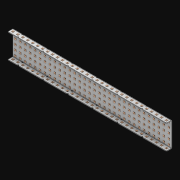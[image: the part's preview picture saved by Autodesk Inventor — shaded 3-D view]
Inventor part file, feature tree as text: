
AUTODESK INVENTOR PART (.ipt)
format: ipt  version: 2021 (Build 250183000, 183)  size: 3,855,872 bytes
history: native  units: in
note: dims shown in document units (in); Inventor stores cm internally (conversion verified against a paired STEP export)
features: extrude x225, other x224, sketch x4, thicken_offset x3, pattern_linear x3, imported_body x1
ambient origin geometry x8: Origin, YZ Plane, XZ Plane, XY Plane, X Axis, Y Axis, Z Axis, Center Point
bodies: Solid1 (feature_tree)
feature tree (460):
  thicken_offset  "Thicken1"
  thicken_offset  "Thicken2"
  thicken_offset  "Thicken3"
  pattern_linear  "Rectangular Pattern1"  Spacing1=0.001in  [1 undecoded]
  pattern_linear  "Rectangular Pattern2"  Spacing1=0.001in  [1 undecoded]
  pattern_linear  "Rectangular Pattern3"  Spacing1=0.182in  [1 undecoded]
  extrude  "Extrusion1"  Depth=0.063in TaperAngle=0.0deg
  sketch  "Sketch1"  dims[d0=0.001in]
  other  "Srf1"
  sketch  "Sketch2"  dims[d1=0.001in]
  other  "Srf2"
  sketch  "Sketch3"  dims[d2=0.001in]
  other  "Srf3"
  other  "Srf4"
  other  "Srf5"
  other  "Srf6"
  other  "Srf7"
  other  "Srf8"
  other  "Srf9"
  other  "Srf10"
  other  "Srf11"
  other  "Srf12"
  other  "Srf13"
  other  "Srf14"
  other  "Srf15"
  other  "Srf16"
  other  "Srf17"
  other  "Srf18"
  other  "Srf19"
  other  "Srf20"
  other  "Srf21"
  other  "Srf22"
  other  "Srf23"
  other  "Srf24"
  other  "Srf25"
  other  "Srf26"
  other  "Srf27"
  other  "Srf28"
  other  "Srf29"
  other  "Srf30"
  other  "Srf31"
  other  "Srf32"
  other  "Srf33"
  other  "Srf34"
  other  "Srf38"
  other  "Srf39"
  other  "Srf40"
  other  "Srf41"
  other  "Srf42"
  other  "Srf43"
  other  "Srf44"
  other  "Srf45"
  other  "Srf46"
  other  "Srf47"
  other  "Srf48"
  other  "Srf49"
  other  "Srf50"
  other  "Srf51"
  other  "Srf52"
  other  "Srf53"
  other  "Srf54"
  other  "Srf55"
  other  "Srf56"
  other  "Srf57"
  other  "Srf58"
  other  "Srf59"
  other  "Srf60"
  other  "Srf61"
  other  "Srf62"
  other  "Srf63"
  other  "Srf64"
  other  "Srf65"
  other  "Srf66"
  other  "Srf67"
  other  "Srf68"
  other  "Srf72"
  other  "Srf73"
  other  "Srf74"
  other  "Srf75"
  other  "Srf76"
  other  "Srf77"
  other  "Srf78"
  other  "Srf79"
  other  "Srf80"
  other  "Srf81"
  other  "Srf82"
  other  "Srf83"
  other  "Srf84"
  other  "Srf85"
  other  "Srf86"
  other  "Srf87"
  other  "Srf88"
  other  "Srf89"
  other  "Srf90"
  other  "Srf91"
  other  "Srf92"
  other  "Srf93"
  other  "Srf94"
  other  "Srf95"
  other  "Srf96"
  other  "Srf97"
  other  "Srf98"
  other  "Srf99"
  other  "Srf100"
  other  "Srf101"
  other  "Srf102"
  other  "Srf106"
  other  "Srf107"
  other  "Srf108"
  other  "Srf109"
  other  "Srf110"
  other  "Srf111"
  other  "Srf112"
  other  "Srf113"
  other  "Srf114"
  other  "Srf115"
  other  "Srf116"
  other  "Srf117"
  other  "Srf118"
  other  "Srf119"
  other  "Srf120"
  other  "Srf121"
  other  "Srf122"
  other  "Srf123"
  other  "Srf124"
  other  "Srf125"
  other  "Srf126"
  other  "Srf127"
  other  "Srf128"
  other  "Srf129"
  other  "Srf130"
  other  "Srf131"
  other  "Srf132"
  other  "Srf133"
  other  "Srf134"
  other  "Srf135"
  other  "Srf136"
  other  "Srf137"
  other  "Srf141"
  other  "Srf142"
  other  "Srf143"
  other  "Srf144"
  other  "Srf145"
  other  "Srf146"
  other  "Srf147"
  other  "Srf148"
  other  "Srf149"
  other  "Srf150"
  other  "Srf151"
  other  "Srf152"
  other  "Srf153"
  other  "Srf154"
  other  "Srf155"
  other  "Srf156"
  other  "Srf157"
  other  "Srf158"
  other  "Srf159"
  other  "Srf160"
  other  "Srf161"
  other  "Srf162"
  other  "Srf163"
  other  "Srf164"
  other  "Srf165"
  other  "Srf166"
  other  "Srf167"
  other  "Srf168"
  other  "Srf169"
  other  "Srf170"
  other  "Srf171"
  other  "Srf172"
  other  "Srf176"
  other  "Srf177"
  other  "Srf178"
  other  "Srf179"
  other  "Srf180"
  other  "Srf181"
  other  "Srf182"
  other  "Srf183"
  other  "Srf184"
  other  "Srf185"
  other  "Srf186"
  other  "Srf187"
  other  "Srf188"
  other  "Srf189"
  other  "Srf190"
  other  "Srf191"
  other  "Srf192"
  other  "Srf193"
  other  "Srf194"
  other  "Srf195"
  other  "Srf196"
  other  "Srf197"
  other  "Srf198"
  other  "Srf199"
  other  "Srf200"
  other  "Srf201"
  other  "Srf202"
  other  "Srf203"
  other  "Srf204"
  other  "Srf205"
  other  "Srf206"
  other  "Srf207"
  other  "Srf211"
  other  "Srf212"
  other  "Srf213"
  other  "Srf214"
  other  "Srf215"
  other  "Srf216"
  other  "Srf217"
  other  "Srf218"
  other  "Srf219"
  other  "Srf220"
  other  "Srf221"
  other  "Srf222"
  other  "Srf223"
  other  "Srf224"
  other  "Srf225"
  other  "Srf226"
  other  "Srf227"
  other  "Srf228"
  other  "Srf229"
  other  "Srf230"
  other  "Srf231"
  other  "Srf232"
  other  "Srf233"
  other  "Srf234"
  other  "Srf235"
  other  "Srf236"
  other  "Srf237"
  other  "Srf238"
  other  "Srf239"
  other  "Srf240"
  other  "Srf241"
  other  "Srf242"
  sketch  "Sketch4"  dims[d3=0.001in d4=0.001in d5=0.001in d6=0.182in d7=0.063in d8=0.0in d9=0.182in d10=0.063in d11=0.0in d12=0.182in d13=0.063in d14=0.0in d17=0.5in d18=12.5984in d20=0.5in d21=12.5984in d23=0.5in d24=1.9685in d26=0.5in d27=1.5in d28=0.0in]
  imported_body  "Imported1"
  extrude  "ExtrusionSrf1"  Depth=1.5in
  extrude  "ExtrusionSrf2"  Depth=0.063in TaperAngle=0.0deg
  extrude  "ExtrusionSrf3"  Depth=1.5in
  extrude  "ExtrusionSrf4"  Depth=0.063in TaperAngle=0.0deg
  extrude  "ExtrusionSrf5"  Depth=0.5in
  extrude  "ExtrusionSrf6"  Depth=1.5in
  extrude  "ExtrusionSrf7"  Depth=0.5in
  extrude  "ExtrusionSrf8"  Depth=1.5in
  extrude  "ExtrusionSrf9"  Depth=0.5in
  extrude  "ExtrusionSrf10"  Depth=0.5in
  extrude  "ExtrusionSrf11"  Depth=1.5in
  extrude  "ExtrusionSrf12"  TaperAngle=0.0deg  [1 undecoded]
  extrude  "ExtrusionSrf13"  [1 undecoded]
  extrude  "ExtrusionSrf14"  [1 undecoded]
  extrude  "ExtrusionSrf15"  [1 undecoded]
  extrude  "ExtrusionSrf16"  [1 undecoded]
  extrude  "ExtrusionSrf17"  [1 undecoded]
  extrude  "ExtrusionSrf18"  [1 undecoded]
  extrude  "ExtrusionSrf19"  [1 undecoded]
  extrude  "ExtrusionSrf20"  [1 undecoded]
  extrude  "ExtrusionSrf21"  [1 undecoded]
  extrude  "ExtrusionSrf22"  [1 undecoded]
  extrude  "ExtrusionSrf23"  [1 undecoded]
  extrude  "ExtrusionSrf24"  [1 undecoded]
  extrude  "ExtrusionSrf25"  [1 undecoded]
  extrude  "ExtrusionSrf26"  [1 undecoded]
  extrude  "ExtrusionSrf27"  [1 undecoded]
  extrude  "ExtrusionSrf28"  [1 undecoded]
  extrude  "ExtrusionSrf29"  [1 undecoded]
  extrude  "ExtrusionSrf30"  [1 undecoded]
  extrude  "ExtrusionSrf31"  [1 undecoded]
  extrude  "ExtrusionSrf32"  [1 undecoded]
  extrude  "ExtrusionSrf33"  [1 undecoded]
  extrude  "ExtrusionSrf34"  [1 undecoded]
  extrude  "ExtrusionSrf38"  [1 undecoded]
  extrude  "ExtrusionSrf39"  [1 undecoded]
  extrude  "ExtrusionSrf40"  [1 undecoded]
  extrude  "ExtrusionSrf41"  [1 undecoded]
  extrude  "ExtrusionSrf42"  [1 undecoded]
  extrude  "ExtrusionSrf43"  [1 undecoded]
  extrude  "ExtrusionSrf44"  [1 undecoded]
  extrude  "ExtrusionSrf45"  [1 undecoded]
  extrude  "ExtrusionSrf46"  [1 undecoded]
  extrude  "ExtrusionSrf47"  [1 undecoded]
  extrude  "ExtrusionSrf48"  [1 undecoded]
  extrude  "ExtrusionSrf49"  [1 undecoded]
  extrude  "ExtrusionSrf50"  [1 undecoded]
  extrude  "ExtrusionSrf51"  [1 undecoded]
  extrude  "ExtrusionSrf52"  [1 undecoded]
  extrude  "ExtrusionSrf53"  [1 undecoded]
  extrude  "ExtrusionSrf54"  [1 undecoded]
  extrude  "ExtrusionSrf55"  [1 undecoded]
  extrude  "ExtrusionSrf56"  [1 undecoded]
  extrude  "ExtrusionSrf57"  [1 undecoded]
  extrude  "ExtrusionSrf58"  [1 undecoded]
  extrude  "ExtrusionSrf59"  [1 undecoded]
  extrude  "ExtrusionSrf60"  [1 undecoded]
  extrude  "ExtrusionSrf61"  [1 undecoded]
  extrude  "ExtrusionSrf62"  [1 undecoded]
  extrude  "ExtrusionSrf63"  [1 undecoded]
  extrude  "ExtrusionSrf64"  [1 undecoded]
  extrude  "ExtrusionSrf65"  [1 undecoded]
  extrude  "ExtrusionSrf66"  [1 undecoded]
  extrude  "ExtrusionSrf67"  [1 undecoded]
  extrude  "ExtrusionSrf68"  [1 undecoded]
  extrude  "ExtrusionSrf72"  [1 undecoded]
  extrude  "ExtrusionSrf73"  [1 undecoded]
  extrude  "ExtrusionSrf74"  [1 undecoded]
  extrude  "ExtrusionSrf75"  [1 undecoded]
  extrude  "ExtrusionSrf76"  [1 undecoded]
  extrude  "ExtrusionSrf77"  [1 undecoded]
  extrude  "ExtrusionSrf78"  [1 undecoded]
  extrude  "ExtrusionSrf79"  [1 undecoded]
  extrude  "ExtrusionSrf80"  [1 undecoded]
  extrude  "ExtrusionSrf81"  [1 undecoded]
  extrude  "ExtrusionSrf82"  [1 undecoded]
  extrude  "ExtrusionSrf83"  [1 undecoded]
  extrude  "ExtrusionSrf84"  [1 undecoded]
  extrude  "ExtrusionSrf85"  [1 undecoded]
  extrude  "ExtrusionSrf86"  [1 undecoded]
  extrude  "ExtrusionSrf87"  [1 undecoded]
  extrude  "ExtrusionSrf88"  [1 undecoded]
  extrude  "ExtrusionSrf89"  [1 undecoded]
  extrude  "ExtrusionSrf90"  [1 undecoded]
  extrude  "ExtrusionSrf91"  [1 undecoded]
  extrude  "ExtrusionSrf92"  [1 undecoded]
  extrude  "ExtrusionSrf93"  [1 undecoded]
  extrude  "ExtrusionSrf94"  [1 undecoded]
  extrude  "ExtrusionSrf95"  [1 undecoded]
  extrude  "ExtrusionSrf96"  [1 undecoded]
  extrude  "ExtrusionSrf97"  [1 undecoded]
  extrude  "ExtrusionSrf98"  [1 undecoded]
  extrude  "ExtrusionSrf99"  [1 undecoded]
  extrude  "ExtrusionSrf100"  [1 undecoded]
  extrude  "ExtrusionSrf101"  [1 undecoded]
  extrude  "ExtrusionSrf102"  [1 undecoded]
  extrude  "ExtrusionSrf106"  [1 undecoded]
  extrude  "ExtrusionSrf107"  [1 undecoded]
  extrude  "ExtrusionSrf108"  [1 undecoded]
  extrude  "ExtrusionSrf109"  [1 undecoded]
  extrude  "ExtrusionSrf110"  [1 undecoded]
  extrude  "ExtrusionSrf111"  [1 undecoded]
  extrude  "ExtrusionSrf112"  [1 undecoded]
  extrude  "ExtrusionSrf113"  [1 undecoded]
  extrude  "ExtrusionSrf114"  [1 undecoded]
  extrude  "ExtrusionSrf115"  [1 undecoded]
  extrude  "ExtrusionSrf116"  [1 undecoded]
  extrude  "ExtrusionSrf117"  [1 undecoded]
  extrude  "ExtrusionSrf118"  [1 undecoded]
  extrude  "ExtrusionSrf119"  [1 undecoded]
  extrude  "ExtrusionSrf120"  [1 undecoded]
  extrude  "ExtrusionSrf121"  [1 undecoded]
  extrude  "ExtrusionSrf122"  [1 undecoded]
  extrude  "ExtrusionSrf123"  [1 undecoded]
  extrude  "ExtrusionSrf124"  [1 undecoded]
  extrude  "ExtrusionSrf125"  [1 undecoded]
  extrude  "ExtrusionSrf126"  [1 undecoded]
  extrude  "ExtrusionSrf127"  [1 undecoded]
  extrude  "ExtrusionSrf128"  [1 undecoded]
  extrude  "ExtrusionSrf129"  [1 undecoded]
  extrude  "ExtrusionSrf130"  [1 undecoded]
  extrude  "ExtrusionSrf131"  [1 undecoded]
  extrude  "ExtrusionSrf132"  [1 undecoded]
  extrude  "ExtrusionSrf133"  [1 undecoded]
  extrude  "ExtrusionSrf134"  [1 undecoded]
  extrude  "ExtrusionSrf135"  [1 undecoded]
  extrude  "ExtrusionSrf136"  [1 undecoded]
  extrude  "ExtrusionSrf137"  [1 undecoded]
  extrude  "ExtrusionSrf141"  [1 undecoded]
  extrude  "ExtrusionSrf142"  [1 undecoded]
  extrude  "ExtrusionSrf143"  [1 undecoded]
  extrude  "ExtrusionSrf144"  [1 undecoded]
  extrude  "ExtrusionSrf145"  [1 undecoded]
  extrude  "ExtrusionSrf146"  [1 undecoded]
  extrude  "ExtrusionSrf147"  [1 undecoded]
  extrude  "ExtrusionSrf148"  [1 undecoded]
  extrude  "ExtrusionSrf149"  [1 undecoded]
  extrude  "ExtrusionSrf150"  [1 undecoded]
  extrude  "ExtrusionSrf151"  [1 undecoded]
  extrude  "ExtrusionSrf152"  [1 undecoded]
  extrude  "ExtrusionSrf153"  [1 undecoded]
  extrude  "ExtrusionSrf154"  [1 undecoded]
  extrude  "ExtrusionSrf155"  [1 undecoded]
  extrude  "ExtrusionSrf156"  [1 undecoded]
  extrude  "ExtrusionSrf157"  [1 undecoded]
  extrude  "ExtrusionSrf158"  [1 undecoded]
  extrude  "ExtrusionSrf159"  [1 undecoded]
  extrude  "ExtrusionSrf160"  [1 undecoded]
  extrude  "ExtrusionSrf161"  [1 undecoded]
  extrude  "ExtrusionSrf162"  [1 undecoded]
  extrude  "ExtrusionSrf163"  [1 undecoded]
  extrude  "ExtrusionSrf164"  [1 undecoded]
  extrude  "ExtrusionSrf165"  [1 undecoded]
  extrude  "ExtrusionSrf166"  [1 undecoded]
  extrude  "ExtrusionSrf167"  [1 undecoded]
  extrude  "ExtrusionSrf168"  [1 undecoded]
  extrude  "ExtrusionSrf169"  [1 undecoded]
  extrude  "ExtrusionSrf170"  [1 undecoded]
  extrude  "ExtrusionSrf171"  [1 undecoded]
  extrude  "ExtrusionSrf172"  [1 undecoded]
  extrude  "ExtrusionSrf176"  [1 undecoded]
  extrude  "ExtrusionSrf177"  [1 undecoded]
  extrude  "ExtrusionSrf178"  [1 undecoded]
  extrude  "ExtrusionSrf179"  [1 undecoded]
  extrude  "ExtrusionSrf180"  [1 undecoded]
  extrude  "ExtrusionSrf181"  [1 undecoded]
  extrude  "ExtrusionSrf182"  [1 undecoded]
  extrude  "ExtrusionSrf183"  [1 undecoded]
  extrude  "ExtrusionSrf184"  [1 undecoded]
  extrude  "ExtrusionSrf185"  [1 undecoded]
  extrude  "ExtrusionSrf186"  [1 undecoded]
  extrude  "ExtrusionSrf187"  [1 undecoded]
  extrude  "ExtrusionSrf188"  [1 undecoded]
  extrude  "ExtrusionSrf189"  [1 undecoded]
  extrude  "ExtrusionSrf190"  [1 undecoded]
  extrude  "ExtrusionSrf191"  [1 undecoded]
  extrude  "ExtrusionSrf192"  [1 undecoded]
  extrude  "ExtrusionSrf193"  [1 undecoded]
  extrude  "ExtrusionSrf194"  [1 undecoded]
  extrude  "ExtrusionSrf195"  [1 undecoded]
  extrude  "ExtrusionSrf196"  [1 undecoded]
  extrude  "ExtrusionSrf197"  [1 undecoded]
  extrude  "ExtrusionSrf198"  [1 undecoded]
  extrude  "ExtrusionSrf199"  [1 undecoded]
  extrude  "ExtrusionSrf200"  [1 undecoded]
  extrude  "ExtrusionSrf201"  [1 undecoded]
  extrude  "ExtrusionSrf202"  [1 undecoded]
  extrude  "ExtrusionSrf203"  [1 undecoded]
  extrude  "ExtrusionSrf204"  [1 undecoded]
  extrude  "ExtrusionSrf205"  [1 undecoded]
  extrude  "ExtrusionSrf206"  [1 undecoded]
  extrude  "ExtrusionSrf207"  [1 undecoded]
  extrude  "ExtrusionSrf211"  [1 undecoded]
  extrude  "ExtrusionSrf212"  [1 undecoded]
  extrude  "ExtrusionSrf213"  [1 undecoded]
  extrude  "ExtrusionSrf214"  [1 undecoded]
  extrude  "ExtrusionSrf215"  [1 undecoded]
  extrude  "ExtrusionSrf216"  [1 undecoded]
  extrude  "ExtrusionSrf217"  [1 undecoded]
  extrude  "ExtrusionSrf218"  [1 undecoded]
  extrude  "ExtrusionSrf219"  [1 undecoded]
  extrude  "ExtrusionSrf220"  [1 undecoded]
  extrude  "ExtrusionSrf221"  [1 undecoded]
  extrude  "ExtrusionSrf222"  [1 undecoded]
  extrude  "ExtrusionSrf223"  [1 undecoded]
  extrude  "ExtrusionSrf224"  [1 undecoded]
  extrude  "ExtrusionSrf225"  [1 undecoded]
  extrude  "ExtrusionSrf226"  [1 undecoded]
  extrude  "ExtrusionSrf227"  [1 undecoded]
  extrude  "ExtrusionSrf228"  [1 undecoded]
  extrude  "ExtrusionSrf229"  [1 undecoded]
  extrude  "ExtrusionSrf230"  [1 undecoded]
  extrude  "ExtrusionSrf231"  [1 undecoded]
  extrude  "ExtrusionSrf232"  [1 undecoded]
  extrude  "ExtrusionSrf233"  [1 undecoded]
  extrude  "ExtrusionSrf234"  [1 undecoded]
  extrude  "ExtrusionSrf235"  [1 undecoded]
  extrude  "ExtrusionSrf236"  [1 undecoded]
  extrude  "ExtrusionSrf237"  [1 undecoded]
  extrude  "ExtrusionSrf238"  [1 undecoded]
  extrude  "ExtrusionSrf239"  [1 undecoded]
  extrude  "ExtrusionSrf240"  [1 undecoded]
  extrude  "ExtrusionSrf241"  [1 undecoded]
  extrude  "ExtrusionSrf242"  [1 undecoded]
note: 216 required parameter values undecoded (feature->parameter linkage not recoverable at this tier; creation-order binding heuristic only, values carry confidence <= 0.55)
